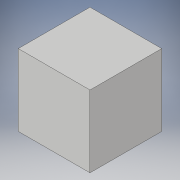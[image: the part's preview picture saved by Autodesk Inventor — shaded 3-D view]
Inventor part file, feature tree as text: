
AUTODESK INVENTOR PART (.ipt)
format: ipt  version: 2019 (Build 230136000, 136)  size: 218,112 bytes
history: native  units: mm
features: extrude x1, sketch x1
ambient origin geometry x8: Origin, YZ Plane, XZ Plane, XY Plane, X Axis, Y Axis, Z Axis, Center Point
bodies: Solid1 (feature_tree)
feature tree (2):
  extrude  "Extrusion1"  Depth=25.0mm
  sketch  "Sketch1"  dims[d0=25.0mm d1=25.0mm d2=25.0mm d3=0.0mm]
